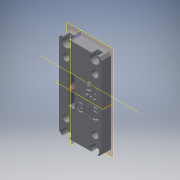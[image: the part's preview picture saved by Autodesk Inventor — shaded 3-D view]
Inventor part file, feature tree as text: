
AUTODESK INVENTOR PART (.ipt)
format: ipt  version: 2019.4 (Build 234330000, 330)  size: 436,224 bytes
history: native  units: mm
features: sketch x7, extrude x6, projected_geometry x5, plane x4, other x3, hole x1, reference x1
ambient origin geometry x8: Origin, YZ Plane, XZ Plane, XY Plane, X Axis, Y Axis, Z Axis, Center Point
bodies: Volumenkörper1 (feature_tree)
feature tree (27):
  plane  "Arbeitsebene1"
  extrude  "Extrusion1"  Depth=1.0mm TaperAngle=0.0deg
  hole  "Bohrung1"  [1 undecoded]
  extrude  "Extrusion3"  Depth=10.0mm
  extrude  "Extrusion4"  Depth=10.0mm
  extrude  "Extrusion5"  Depth=22.0mm
  extrude  "Extrusion6"  Depth=1.0mm
  extrude  "Extrusion7"  Depth=3.0mm
  plane  "Work Plane2"
  plane  "Work Plane3"
  plane  "Work Plane4"
  sketch  "Skizze1"  dims[d0=4.0mm d1=0.0mm]
  reference  "Referenz1"
  sketch  "Skizze2"  dims[d2=2.0mm d3=6.0mm d4=4.0mm d5=2.5mm d6=90.0deg d7=12.0mm d8=20.594885mm d28=1.0mm d29=0.0mm]
  projected_geometry  "Projizierte Kontur1"
  sketch  "Skizze5"  dims[d31=12.3mm d32=2.5mm]
  sketch  "Skizze6"  dims[d33=10.0mm d34=0.0mm d35=2.8mm]
  projected_geometry  "Projizierte Kontur4"
  sketch  "Skizze7"  dims[d36=10.0mm d37=0.0mm d38=17.9mm]
  projected_geometry  "Projizierte Kontur5"
  sketch  "Skizze8"  dims[d39=12.0mm d40=22.0mm]
  projected_geometry  "Projizierte Kontur6"
  sketch  "Skizze9"  dims[d41=17.9mm d42=8.9mm d43=3.0mm d44=3.0mm d45=3.0mm d46=3.0mm d47=3.0mm d48=-0.698132mm d49=0.4mm d50=1.0mm d51=0.0mm]
  projected_geometry  "Projizierte Kontur7"
  other  "Assembly_Omniscope_v1.iam"
  other  "01_Camera_Module_left_v0:1"
  other  "<userpath>\Documents\Inventor\HITscope\Assembly_Omniscope_v1.iam"
note: 1 required parameter value undecoded (feature->parameter linkage not recoverable at this tier; creation-order binding heuristic only, values carry confidence <= 0.55)
